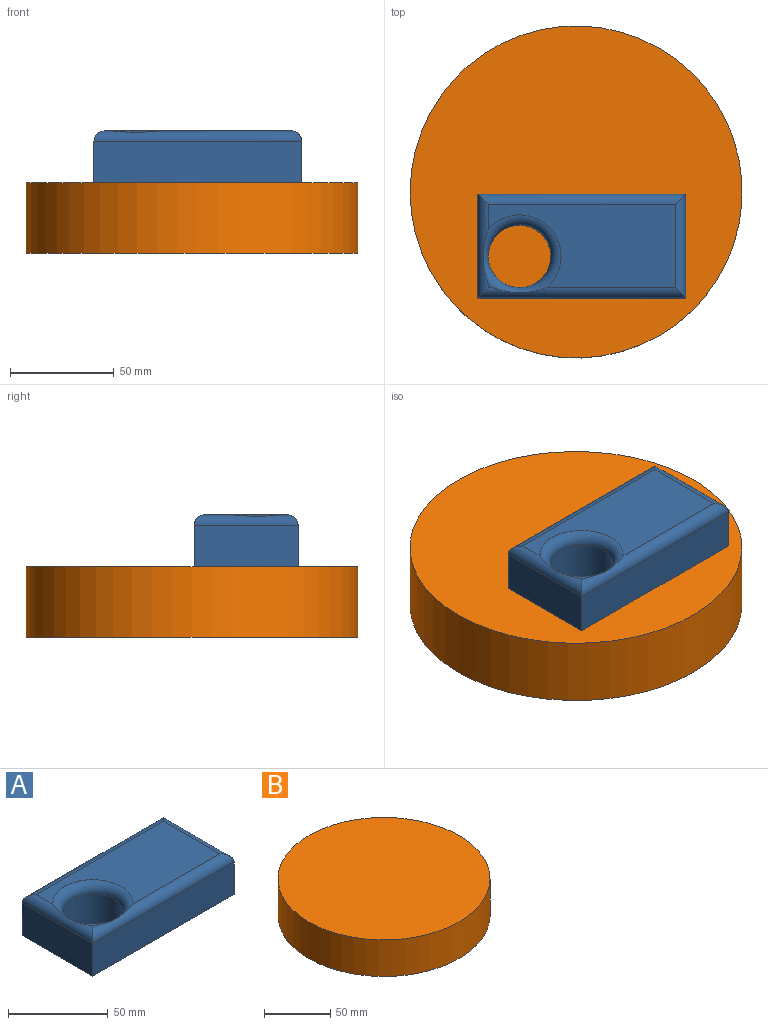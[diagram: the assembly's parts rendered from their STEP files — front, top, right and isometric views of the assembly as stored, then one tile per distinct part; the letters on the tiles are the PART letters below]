
ASSEMBLY  parts=2 mates=1
PART A: 13 faces, bbox 105.5x55.5x25 mm
  f0: plane 1.77x1.77mm, normal (0,0,1), area 1.5mm2, adj f10,f11,f12
  f1: plane 100x20mm, normal (0,1,0), area 2000mm2, adj f2,f4,f6,f8
  f2: plane 50x20mm, normal (-1,0,0), area 1000mm2, adj f1,f3,f6,f10
  f3: plane 100x20mm, normal (0,-1,0), area 2000mm2, adj f2,f4,f6,f11
  f4: plane 50x20mm, normal (1,0,0), area 1000mm2, adj f1,f3,f6,f9
  f5: plane 90x40mm, normal (0,0,1), area 2523.2mm2, adj f8,f9,f10,f11,f12
  f6: plane 100x50mm, normal (0,0,-1), area 4293.1mm2, adj f1,f2,f3,f4,f7
  f7: cylinder r=15mm len=30mm, axis (0,0,1), area 1885mm2, adj f6,f12
  f8: cylinder r=5mm len=100mm, axis (1,0,0), area 756.9mm2, adj f1,f5,f9,f10
  f9: cylinder r=5mm len=50mm, axis (0,-1,0), area 364.2mm2, adj f4,f5,f8,f11
  f10: cylinder r=5mm len=50mm, axis (0,1,0), area 318.7mm2, adj f0,f2,f5,f8,f11,f12
  f11: cylinder r=5mm len=100mm, axis (-1,0,0), area 711.4mm2, adj f0,f3,f5,f9,f10,f12
  f12: torus R=20mm, axis (0,0,1), area 733.9mm2, adj f0,f5,f7,f10,f11
PART B: 3 faces, bbox 159.8x159.8x33.8 mm
  f0: plane 159.83x159.83mm, normal (0,0,1), area 20062.6mm2, adj f2
  f1: plane 159.83x159.83mm, normal (0,0,-1), area 20062.6mm2, adj f2
  f2: cylinder r=79.91mm len=159.83mm, axis (0,0,-1), area 16956.3mm2, adj f0,f1
PLACE A t=(-33.07,-52.25,-1.66)mm
PLACE B t=(14.18,-1.19,-35.43)mm
MATE planar A.f6 <-> B.f2  axis (0,0,-1) through (16.93,-2.25,-1.66)mm
